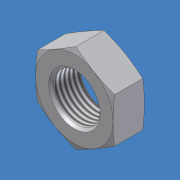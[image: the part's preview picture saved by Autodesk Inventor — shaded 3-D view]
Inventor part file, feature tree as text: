
AUTODESK INVENTOR PART (.ipt)
format: ipt  version: 2012 (Build 160160000, 160)  size: 129,536 bytes
history: native  units: mm (DEFAULTED — no unit token found)
features: other x70, sketch x3, revolve x2, extrude x1, thread x1
ambient origin geometry x8: Origin, YZ Plane, XZ Plane, XY Plane, X Axis, Y Axis, Z Axis, Center Point
bodies: Solid1 (feature_tree)
feature tree (77):
  sketch  "Sketch_8"  dims[d0=360.0deg d1=9.652mm d2=0.0mm]
  sketch  "Sketch_10"  dims[d3=360.0deg d4=8.12546mm d5=0.0mm]
  revolve  "Revolution1"  [1 undecoded]
  extrude  "Extrusion1"  Depth=8.12546mm TaperAngle=0.0deg
  revolve  "Revolution2"  [1 undecoded]
  thread  "Thread1"  [1 undecoded]
  other  "NUT_XY"
  other  "NUT_YZ"
  other  "NUT_ZX"
  other  "NUT_X"
  other  "NUT_Y"
  other  "NUT_Z"
  other  "NUT_Center"
  other  "a1_XY"
  other  "a1_YZ"
  other  "a1_ZX"
  other  "a1_X"
  other  "a1_Y"
  other  "a1_Z"
  other  "a1_Center"
  other  "a2_XY"
  other  "a2_YZ"
  other  "a2_ZX"
  other  "a2_X"
  other  "a2_Y"
  other  "a2_Z"
  other  "a2_Center"
  other  "b1_XY"
  other  "b1_YZ"
  other  "b1_ZX"
  other  "b1_X"
  other  "b1_Y"
  other  "b1_Z"
  other  "b1_Center"
  other  "b2_XY"
  other  "b2_YZ"
  other  "b2_ZX"
  other  "b2_X"
  other  "b2_Y"
  other  "b2_Z"
  other  "b2_Center"
  other  "e_XY"
  other  "e_YZ"
  other  "e_ZX"
  other  "e_X"
  other  "e_Y"
  other  "e_Z"
  other  "e_Center"
  other  "th1_XY"
  other  "th1_YZ"
  other  "th1_ZX"
  other  "th1_X"
  other  "th1_Y"
  other  "th1_Z"
  other  "th1_Center"
  other  "th2_XY"
  other  "th2_YZ"
  other  "th2_ZX"
  other  "th2_X"
  other  "th2_Y"
  other  "th2_Z"
  other  "th2_Center"
  other  "ol1_XY"
  other  "ol1_YZ"
  other  "ol1_ZX"
  other  "ol1_X"
  other  "ol1_Y"
  other  "ol1_Z"
  other  "ol1_Center"
  other  "ol2_XY"
  other  "ol2_YZ"
  other  "ol2_ZX"
  other  "ol2_X"
  other  "ol2_Y"
  other  "ol2_Z"
  other  "ol2_Center"
  sketch  "Sketch_11"
note: 3 required parameter values undecoded (feature->parameter linkage not recoverable at this tier; creation-order binding heuristic only, values carry confidence <= 0.55)